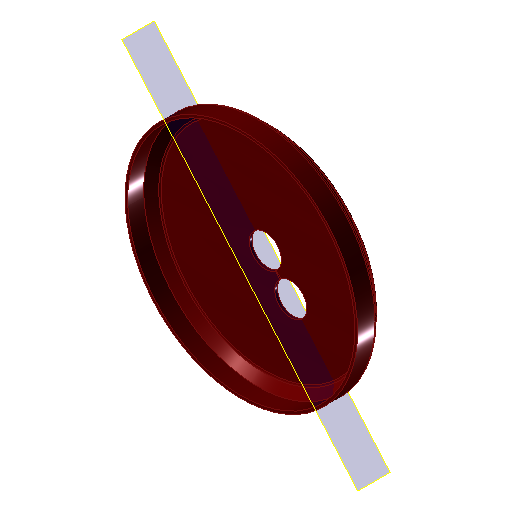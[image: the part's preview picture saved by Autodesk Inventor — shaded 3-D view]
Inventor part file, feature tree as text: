
AUTODESK INVENTOR PART (.ipt)
format: ipt  version: 2022 (Build 260153000, 153)  size: 200,192 bytes
history: native  units: mm
features: other x3, sketch x2, reference x2, revolve x1, fillet x1, extrude x1, plane x1
ambient origin geometry x8: Origin, YZ Plane, XZ Plane, XY Plane, X Axis, Y Axis, Z Axis, Center Point
bodies: Volumenkörper1 (feature_tree)
feature tree (11):
  revolve  "Umdrehung1"
  fillet  "Rundung1"  Radius=34.25mm
  extrude  "Extrusion1"  Depth=6.0mm
  plane  "Arbeitsebene1"
  sketch  "Skizze1"  dims[d1=1.0mm d2=6.0mm]
  sketch  "Skizze2"  dims[d3=10.0mm d4=1.0mm d5=1.0mm d6=90.0deg d7=1.0mm d8=12.0mm d9=12.0mm d10=10.0mm d11=0.0mm]
  reference  "Referenz1"
  reference  "Referenz2"
  other  "Anglerfish_bonne_mamman_m12large_flipped_v0.iam"
  other  "Anglerfish_Lightplate_Tislinkbridge:1"
  other  "Anglerfish_flipped_LidMoun:1"
